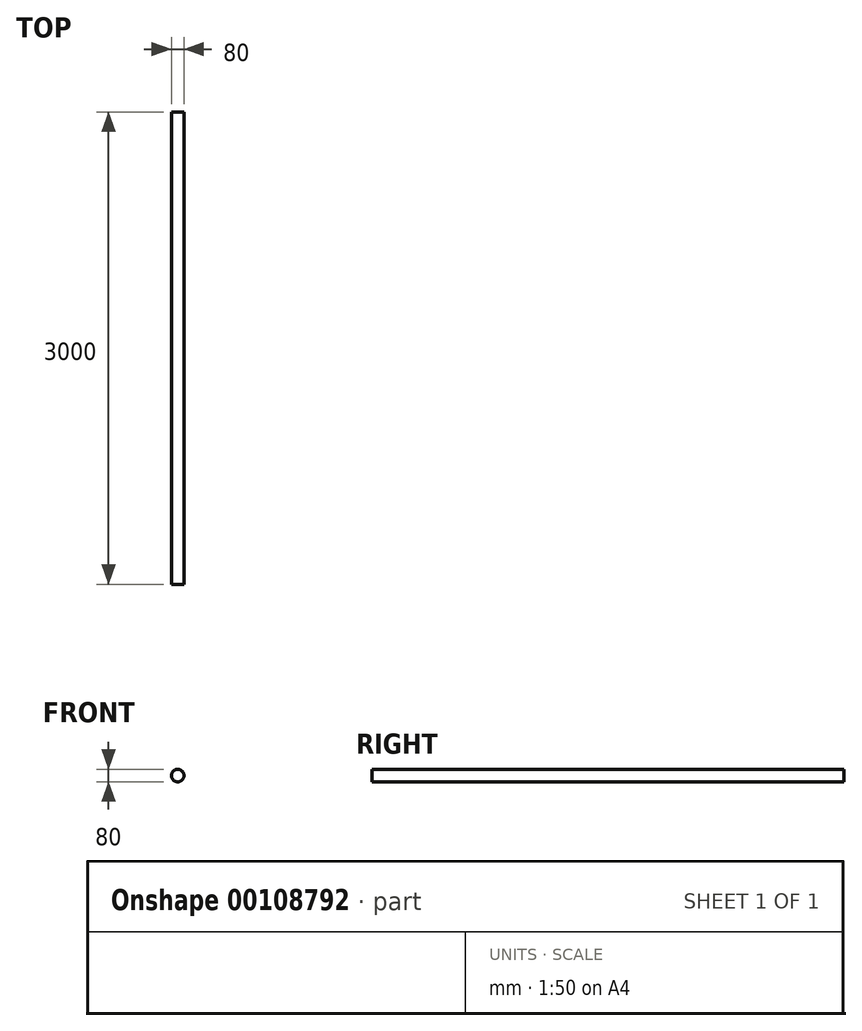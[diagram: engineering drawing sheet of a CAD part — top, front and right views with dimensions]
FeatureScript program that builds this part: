
annotation { "Feature Type Name" : "Feature", "Feature Type Description" : "" }
export const myFeature = defineFeature(function(context is Context, id is Id, definition is map)
    precondition{}
    {
        {
            var Q0;
            Q0=qCreatedBy(makeId("Front.planeOp"),FACE);
            var sketch = newSketch(context, id + "F0", { "sketchPlane" : qUnion([Q0])});
            skCircle(sketch, "E0", {"center": v(0, 0) * mm, "radius": 40 * mm});
            skSolve(sketch);
        }
        {
            var Q0;
            Q0 = qSketchRegion(id + "F0", true);
            extrude(context, id + "F1", {"entities" : qUnion([Q0]), "depth" : 3000 * mm});
        }
    });
